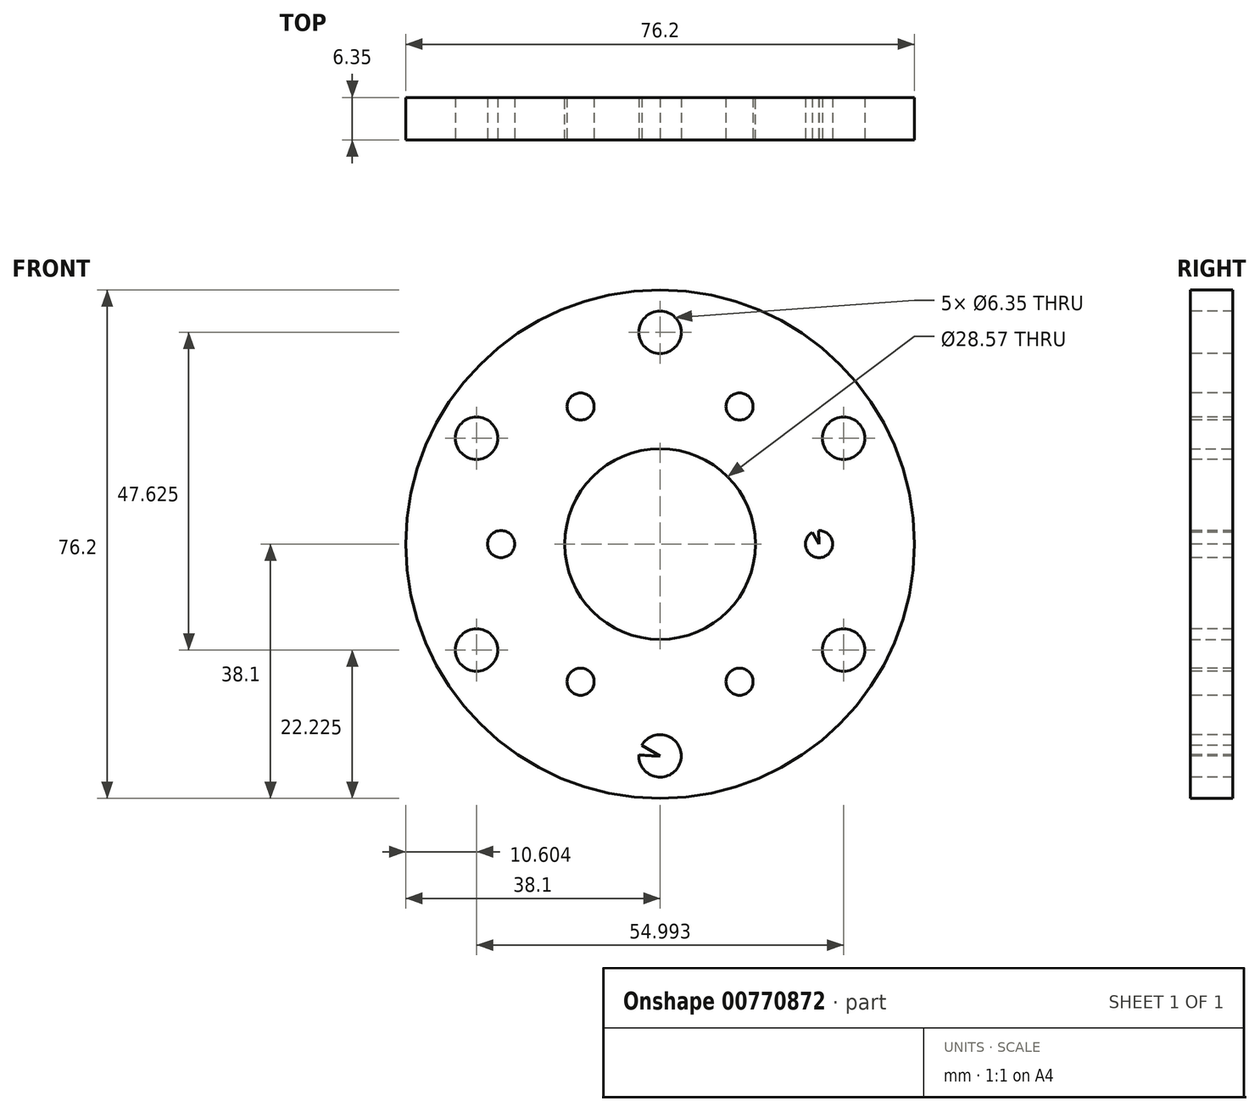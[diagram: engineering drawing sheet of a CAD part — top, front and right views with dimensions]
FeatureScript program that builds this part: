
annotation { "Feature Type Name" : "Feature", "Feature Type Description" : "" }
export const myFeature = defineFeature(function(context is Context, id is Id, definition is map)
    precondition{}
    {
        {
            var Q0;
            Q0=qCreatedBy(makeId("Front.planeOp"),FACE);
            var sketch = newSketch(context, id + "F0", { "sketchPlane" : qUnion([Q0])});
            skCircle(sketch, "E0", {"center": v(0, 0) * mm, "radius": 14.29 * mm});
            skCircle(sketch, "E1", {"center": v(0, 0) * mm, "radius": 38.1 * mm});
            skSolve(sketch);
        }
        {
            var Q0;
            Q0 = qSketchRegion(id + "F0", true);
            extrude(context, id + "F1", {"entities" : qUnion([Q0]), "depth" : 6.35 * mm, "offsetDistance" : 25.4 * mm});
        }
        {
            var Q0;
            Q0=makeQuery(id+"F1.opExtrude","CAP_FACE",FACE,{"disambiguationData":[OSD([sQuery(id+"F0.wireOp",EDGE,"E0"),sQuery(id+"F0.wireOp",EDGE,"E1")])],"isStart":false});
            var sketch = newSketch(context, id + "F2", { "sketchPlane" : qUnion([Q0])});
            skCircle(sketch, "E2", {"center": v(0, 0) * mm, "radius": 23.81 * mm});
            skCircle(sketch, "E3", {"center": v(0, 0) * mm, "radius": 31.75 * mm});
            skCircle(sketch, "E4.cCircle", {"center": v(0, 0) * mm, "radius": 31.75 * mm, "construction": true});
            skLineSegment(sketch, "E4.0", {"start": v(0, 31.75) * mm, "end": v(27.5, 15.88) * mm});
            skLineSegment(sketch, "E4.1", {"start": v(27.5, 15.88) * mm, "end": v(27.5, -15.87) * mm});
            skLineSegment(sketch, "E4.2", {"start": v(27.5, -15.87) * mm, "end": v(0, -31.75) * mm});
            skLineSegment(sketch, "E4.3", {"start": v(0, -31.75) * mm, "end": v(-27.5, -15.88) * mm});
            skLineSegment(sketch, "E4.4", {"start": v(-27.5, -15.88) * mm, "end": v(-27.5, 15.87) * mm});
            skLineSegment(sketch, "E4.5", {"start": v(-27.5, 15.87) * mm, "end": v(0, 31.75) * mm});
            skCircle(sketch, "E5.cCircle", {"center": v(0, 0) * mm, "radius": 23.81 * mm, "construction": true});
            skLineSegment(sketch, "E5.0", {"start": v(-23.81, 0) * mm, "end": v(-11.9, 20.62) * mm});
            skLineSegment(sketch, "E5.1", {"start": v(-11.9, 20.62) * mm, "end": v(11.9, 20.62) * mm});
            skLineSegment(sketch, "E5.2", {"start": v(11.9, 20.62) * mm, "end": v(23.81, 0) * mm});
            skLineSegment(sketch, "E5.3", {"start": v(23.81, 0) * mm, "end": v(11.9, -20.62) * mm});
            skLineSegment(sketch, "E5.4", {"start": v(11.9, -20.62) * mm, "end": v(-11.9, -20.62) * mm});
            skLineSegment(sketch, "E5.5", {"start": v(-11.9, -20.62) * mm, "end": v(-23.81, 0) * mm});
            skCircle(sketch, "E6", {"center": v(0, 31.75) * mm, "radius": 3.18 * mm});
            skCircle(sketch, "E7", {"center": v(27.5, 15.88) * mm, "radius": 3.18 * mm});
            skCircle(sketch, "E8", {"center": v(27.5, -15.87) * mm, "radius": 3.18 * mm});
            skCircle(sketch, "E9", {"center": v(0, -31.75) * mm, "radius": 3.18 * mm});
            skCircle(sketch, "E10", {"center": v(-27.5, -15.88) * mm, "radius": 3.18 * mm});
            skCircle(sketch, "E11", {"center": v(-27.5, 15.87) * mm, "radius": 3.18 * mm});
            skCircle(sketch, "E12", {"center": v(-11.9, 20.62) * mm, "radius": 2.03 * mm});
            skCircle(sketch, "E13", {"center": v(11.9, 20.62) * mm, "radius": 2.03 * mm});
            skCircle(sketch, "E14", {"center": v(23.81, 0) * mm, "radius": 2.03 * mm});
            skCircle(sketch, "E15", {"center": v(11.9, -20.62) * mm, "radius": 2.03 * mm});
            skCircle(sketch, "E16", {"center": v(-11.9, -20.62) * mm, "radius": 2.03 * mm});
            skCircle(sketch, "E17", {"center": v(-23.81, 0) * mm, "radius": 2.03 * mm});
            skSolve(sketch);
        }
        {
            var Q0;
            {var subQ0=sQuery(id+"F2.wireOp",EDGE,"E3");var subQ2=sQuery(id+"F2.wireOp",EDGE,"E7");var subQ3=makeQuery(id+"F2.imprint","INTERSECT",VERTEX,{"disambiguationData":[OD(0.0)],"derivedFrom":[subQ0,subQ2]});Q0=makeQuery(id+"F2.imprint","IMPRINT",FACE,{"disambiguationData":[TD([[makeQuery(id+"F2.imprint","IMPRINT",EDGE,{"disambiguationData":[TD([[subQ3,-1.0]])],"derivedFrom":subQ2}),1.0]])]});}
            var Q1;
            {var subQ1=sQuery(id+"F2.wireOp",EDGE,"E3");var subQ3=sQuery(id+"F2.wireOp",EDGE,"E7");var subQ4=makeQuery(id+"F2.imprint","INTERSECT",VERTEX,{"disambiguationData":[OD(0.0)],"derivedFrom":[subQ1,subQ3]});Q1=makeQuery(id+"F2.imprint","IMPRINT",FACE,{"disambiguationData":[TD([[makeQuery(id+"F2.imprint","IMPRINT",EDGE,{"disambiguationData":[TD([[subQ4,1.0]])],"derivedFrom":subQ3}),1.0]])]});}
            var Q2;
            {var subQ1=sQuery(id+"F2.wireOp",EDGE,"E3");var subQ3=sQuery(id+"F2.wireOp",EDGE,"E7");var subQ4=makeQuery(id+"F2.imprint","INTERSECT",VERTEX,{"disambiguationData":[OD(1.0)],"derivedFrom":[subQ1,subQ3]});Q2=makeQuery(id+"F2.imprint","IMPRINT",FACE,{"disambiguationData":[TD([[makeQuery(id+"F2.imprint","IMPRINT",EDGE,{"disambiguationData":[TD([[subQ4,-1.0]])],"derivedFrom":subQ3}),1.0]])]});}
            var Q3;
            {var subQ0=sQuery(id+"F2.wireOp",EDGE,"E3");var subQ2=sQuery(id+"F2.wireOp",EDGE,"E6");var subQ3=makeQuery(id+"F2.imprint","INTERSECT",VERTEX,{"disambiguationData":[OD(0.0)],"derivedFrom":[subQ0,subQ2]});Q3=makeQuery(id+"F2.imprint","IMPRINT",FACE,{"disambiguationData":[TD([[makeQuery(id+"F2.imprint","IMPRINT",EDGE,{"disambiguationData":[TD([[subQ3,-1.0]])],"derivedFrom":subQ2}),1.0]])]});}
            var Q4;
            {var subQ1=sQuery(id+"F2.wireOp",EDGE,"E3");var subQ3=sQuery(id+"F2.wireOp",EDGE,"E6");var subQ4=makeQuery(id+"F2.imprint","INTERSECT",VERTEX,{"disambiguationData":[OD(0.0)],"derivedFrom":[subQ1,subQ3]});Q4=makeQuery(id+"F2.imprint","IMPRINT",FACE,{"disambiguationData":[TD([[makeQuery(id+"F2.imprint","IMPRINT",EDGE,{"disambiguationData":[TD([[subQ4,1.0]])],"derivedFrom":subQ3}),1.0]])]});}
            var Q5;
            {var subQ1=sQuery(id+"F2.wireOp",EDGE,"E3");var subQ3=sQuery(id+"F2.wireOp",EDGE,"E6");var subQ4=makeQuery(id+"F2.imprint","INTERSECT",VERTEX,{"disambiguationData":[OD(1.0)],"derivedFrom":[subQ1,subQ3]});Q5=makeQuery(id+"F2.imprint","IMPRINT",FACE,{"disambiguationData":[TD([[makeQuery(id+"F2.imprint","IMPRINT",EDGE,{"disambiguationData":[TD([[subQ4,-1.0]])],"derivedFrom":subQ3}),1.0]])]});}
            var Q6;
            {var subQ0=sQuery(id+"F2.wireOp",EDGE,"E3");var subQ2=sQuery(id+"F2.wireOp",EDGE,"E11");var subQ3=makeQuery(id+"F2.imprint","INTERSECT",VERTEX,{"disambiguationData":[OD(0.0)],"derivedFrom":[subQ0,subQ2]});Q6=makeQuery(id+"F2.imprint","IMPRINT",FACE,{"disambiguationData":[TD([[makeQuery(id+"F2.imprint","IMPRINT",EDGE,{"disambiguationData":[TD([[subQ3,-1.0]])],"derivedFrom":subQ2}),1.0]])]});}
            var Q7;
            {var subQ1=sQuery(id+"F2.wireOp",EDGE,"E3");var subQ3=sQuery(id+"F2.wireOp",EDGE,"E11");var subQ4=makeQuery(id+"F2.imprint","INTERSECT",VERTEX,{"disambiguationData":[OD(0.0)],"derivedFrom":[subQ1,subQ3]});Q7=makeQuery(id+"F2.imprint","IMPRINT",FACE,{"disambiguationData":[TD([[makeQuery(id+"F2.imprint","IMPRINT",EDGE,{"disambiguationData":[TD([[subQ4,1.0]])],"derivedFrom":subQ3}),1.0]])]});}
            var Q8;
            {var subQ1=sQuery(id+"F2.wireOp",EDGE,"E3");var subQ3=sQuery(id+"F2.wireOp",EDGE,"E11");var subQ4=makeQuery(id+"F2.imprint","INTERSECT",VERTEX,{"disambiguationData":[OD(1.0)],"derivedFrom":[subQ1,subQ3]});Q8=makeQuery(id+"F2.imprint","IMPRINT",FACE,{"disambiguationData":[TD([[makeQuery(id+"F2.imprint","IMPRINT",EDGE,{"disambiguationData":[TD([[subQ4,-1.0]])],"derivedFrom":subQ3}),1.0]])]});}
            var Q9;
            {var subQ0=sQuery(id+"F2.wireOp",EDGE,"E3");var subQ2=sQuery(id+"F2.wireOp",EDGE,"E10");var subQ3=makeQuery(id+"F2.imprint","INTERSECT",VERTEX,{"disambiguationData":[OD(0.0)],"derivedFrom":[subQ0,subQ2]});Q9=makeQuery(id+"F2.imprint","IMPRINT",FACE,{"disambiguationData":[TD([[makeQuery(id+"F2.imprint","IMPRINT",EDGE,{"disambiguationData":[TD([[subQ3,-1.0]])],"derivedFrom":subQ2}),1.0]])]});}
            var Q10;
            {var subQ1=sQuery(id+"F2.wireOp",EDGE,"E3");var subQ3=sQuery(id+"F2.wireOp",EDGE,"E10");var subQ4=makeQuery(id+"F2.imprint","INTERSECT",VERTEX,{"disambiguationData":[OD(0.0)],"derivedFrom":[subQ1,subQ3]});Q10=makeQuery(id+"F2.imprint","IMPRINT",FACE,{"disambiguationData":[TD([[makeQuery(id+"F2.imprint","IMPRINT",EDGE,{"disambiguationData":[TD([[subQ4,1.0]])],"derivedFrom":subQ3}),1.0]])]});}
            var Q11;
            {var subQ1=sQuery(id+"F2.wireOp",EDGE,"E3");var subQ3=sQuery(id+"F2.wireOp",EDGE,"E10");var subQ4=makeQuery(id+"F2.imprint","INTERSECT",VERTEX,{"disambiguationData":[OD(1.0)],"derivedFrom":[subQ1,subQ3]});Q11=makeQuery(id+"F2.imprint","IMPRINT",FACE,{"disambiguationData":[TD([[makeQuery(id+"F2.imprint","IMPRINT",EDGE,{"disambiguationData":[TD([[subQ4,-1.0]])],"derivedFrom":subQ3}),1.0]])]});}
            var Q12;
            {var subQ0=sQuery(id+"F2.wireOp",EDGE,"E3");var subQ2=sQuery(id+"F2.wireOp",EDGE,"E9");var subQ3=makeQuery(id+"F2.imprint","INTERSECT",VERTEX,{"disambiguationData":[OD(0.0)],"derivedFrom":[subQ0,subQ2]});Q12=makeQuery(id+"F2.imprint","IMPRINT",FACE,{"disambiguationData":[TD([[makeQuery(id+"F2.imprint","IMPRINT",EDGE,{"disambiguationData":[TD([[subQ3,-1.0]])],"derivedFrom":subQ2}),1.0]])]});}
            var Q13;
            {var subQ1=sQuery(id+"F2.wireOp",EDGE,"E3");var subQ3=sQuery(id+"F2.wireOp",EDGE,"E9");var subQ4=makeQuery(id+"F2.imprint","INTERSECT",VERTEX,{"disambiguationData":[OD(0.0)],"derivedFrom":[subQ1,subQ3]});Q13=makeQuery(id+"F2.imprint","IMPRINT",FACE,{"disambiguationData":[TD([[makeQuery(id+"F2.imprint","IMPRINT",EDGE,{"disambiguationData":[TD([[subQ4,1.0]])],"derivedFrom":subQ3}),1.0]])]});}
            var Q14;
            {var subQ1=sQuery(id+"F2.wireOp",EDGE,"E3");var subQ3=sQuery(id+"F2.wireOp",EDGE,"E9");var subQ4=makeQuery(id+"F2.imprint","INTERSECT",VERTEX,{"disambiguationData":[OD(1.0)],"derivedFrom":[subQ1,subQ3]});Q14=makeQuery(id+"F2.imprint","IMPRINT",FACE,{"disambiguationData":[TD([[makeQuery(id+"F2.imprint","IMPRINT",EDGE,{"disambiguationData":[TD([[subQ4,-1.0]])],"derivedFrom":subQ3}),1.0]])]});}
            var Q15;
            {var subQ0=sQuery(id+"F2.wireOp",EDGE,"E3");var subQ2=sQuery(id+"F2.wireOp",EDGE,"E8");var subQ3=makeQuery(id+"F2.imprint","INTERSECT",VERTEX,{"disambiguationData":[OD(0.0)],"derivedFrom":[subQ0,subQ2]});Q15=makeQuery(id+"F2.imprint","IMPRINT",FACE,{"disambiguationData":[TD([[makeQuery(id+"F2.imprint","IMPRINT",EDGE,{"disambiguationData":[TD([[subQ3,-1.0]])],"derivedFrom":subQ2}),1.0]])]});}
            var Q16;
            {var subQ1=sQuery(id+"F2.wireOp",EDGE,"E3");var subQ3=sQuery(id+"F2.wireOp",EDGE,"E8");var subQ4=makeQuery(id+"F2.imprint","INTERSECT",VERTEX,{"disambiguationData":[OD(0.0)],"derivedFrom":[subQ1,subQ3]});Q16=makeQuery(id+"F2.imprint","IMPRINT",FACE,{"disambiguationData":[TD([[makeQuery(id+"F2.imprint","IMPRINT",EDGE,{"disambiguationData":[TD([[subQ4,1.0]])],"derivedFrom":subQ3}),1.0]])]});}
            var Q17;
            {var subQ1=sQuery(id+"F2.wireOp",EDGE,"E3");var subQ3=sQuery(id+"F2.wireOp",EDGE,"E8");var subQ4=makeQuery(id+"F2.imprint","INTERSECT",VERTEX,{"disambiguationData":[OD(1.0)],"derivedFrom":[subQ1,subQ3]});Q17=makeQuery(id+"F2.imprint","IMPRINT",FACE,{"disambiguationData":[TD([[makeQuery(id+"F2.imprint","IMPRINT",EDGE,{"disambiguationData":[TD([[subQ4,-1.0]])],"derivedFrom":subQ3}),1.0]])]});}
            var Q18;
            {var subQ1=sQuery(id+"F2.wireOp",EDGE,"E4.4");var subQ3=sQuery(id+"F2.wireOp",EDGE,"E11");var subQ4=makeQuery(id+"F2.imprint","INTERSECT",VERTEX,{"derivedFrom":[subQ1,subQ3]});Q18=makeQuery(id+"F2.imprint","IMPRINT",FACE,{"disambiguationData":[TD([[makeQuery(id+"F2.imprint","IMPRINT",EDGE,{"disambiguationData":[TD([[subQ4,-1.0]])],"derivedFrom":subQ3}),1.0]])]});}
            var Q19;
            {var subQ1=sQuery(id+"F2.wireOp",EDGE,"E4.3");var subQ3=sQuery(id+"F2.wireOp",EDGE,"E10");var subQ4=makeQuery(id+"F2.imprint","INTERSECT",VERTEX,{"derivedFrom":[subQ1,subQ3]});Q19=makeQuery(id+"F2.imprint","IMPRINT",FACE,{"disambiguationData":[TD([[makeQuery(id+"F2.imprint","IMPRINT",EDGE,{"disambiguationData":[TD([[subQ4,-1.0]])],"derivedFrom":subQ3}),1.0]])]});}
            var Q20;
            {var subQ1=sQuery(id+"F2.wireOp",EDGE,"E4.2");var subQ3=sQuery(id+"F2.wireOp",EDGE,"E9");var subQ4=makeQuery(id+"F2.imprint","INTERSECT",VERTEX,{"derivedFrom":[subQ1,subQ3]});Q20=makeQuery(id+"F2.imprint","IMPRINT",FACE,{"disambiguationData":[TD([[makeQuery(id+"F2.imprint","IMPRINT",EDGE,{"disambiguationData":[TD([[subQ4,-1.0]])],"derivedFrom":subQ3}),1.0]])]});}
            var Q21;
            {var subQ1=sQuery(id+"F2.wireOp",EDGE,"E4.1");var subQ3=sQuery(id+"F2.wireOp",EDGE,"E8");var subQ4=makeQuery(id+"F2.imprint","INTERSECT",VERTEX,{"derivedFrom":[subQ1,subQ3]});Q21=makeQuery(id+"F2.imprint","IMPRINT",FACE,{"disambiguationData":[TD([[makeQuery(id+"F2.imprint","IMPRINT",EDGE,{"disambiguationData":[TD([[subQ4,-1.0]])],"derivedFrom":subQ3}),1.0]])]});}
            var Q22;
            {var subQ1=sQuery(id+"F2.wireOp",EDGE,"E4.0");var subQ3=sQuery(id+"F2.wireOp",EDGE,"E7");var subQ4=makeQuery(id+"F2.imprint","INTERSECT",VERTEX,{"derivedFrom":[subQ1,subQ3]});Q22=makeQuery(id+"F2.imprint","IMPRINT",FACE,{"disambiguationData":[TD([[makeQuery(id+"F2.imprint","IMPRINT",EDGE,{"disambiguationData":[TD([[subQ4,-1.0]])],"derivedFrom":subQ3}),1.0]])]});}
            var Q23;
            {var subQ1=sQuery(id+"F2.wireOp",EDGE,"E4.0");var subQ3=sQuery(id+"F2.wireOp",EDGE,"E6");var subQ4=makeQuery(id+"F2.imprint","INTERSECT",VERTEX,{"derivedFrom":[subQ1,subQ3]});Q23=makeQuery(id+"F2.imprint","IMPRINT",FACE,{"disambiguationData":[TD([[makeQuery(id+"F2.imprint","IMPRINT",EDGE,{"disambiguationData":[TD([[subQ4,1.0]])],"derivedFrom":subQ3}),1.0]])]});}
            var Q24;
            {var subQ0=sQuery(id+"F2.wireOp",EDGE,"E2");var subQ2=sQuery(id+"F2.wireOp",EDGE,"E12");var subQ3=makeQuery(id+"F2.imprint","INTERSECT",VERTEX,{"disambiguationData":[OD(0.0)],"derivedFrom":[subQ0,subQ2]});Q24=makeQuery(id+"F2.imprint","IMPRINT",FACE,{"disambiguationData":[TD([[makeQuery(id+"F2.imprint","IMPRINT",EDGE,{"disambiguationData":[TD([[subQ3,-1.0]])],"derivedFrom":subQ2}),1.0]])]});}
            var Q25;
            {var subQ1=sQuery(id+"F2.wireOp",EDGE,"E5.0");var subQ3=sQuery(id+"F2.wireOp",EDGE,"E12");var subQ4=makeQuery(id+"F2.imprint","INTERSECT",VERTEX,{"derivedFrom":[subQ1,subQ3]});Q25=makeQuery(id+"F2.imprint","IMPRINT",FACE,{"disambiguationData":[TD([[makeQuery(id+"F2.imprint","IMPRINT",EDGE,{"disambiguationData":[TD([[subQ4,-1.0]])],"derivedFrom":subQ3}),1.0]])]});}
            var Q26;
            {var subQ1=sQuery(id+"F2.wireOp",EDGE,"E2");var subQ3=sQuery(id+"F2.wireOp",EDGE,"E12");var subQ4=makeQuery(id+"F2.imprint","INTERSECT",VERTEX,{"disambiguationData":[OD(0.0)],"derivedFrom":[subQ1,subQ3]});Q26=makeQuery(id+"F2.imprint","IMPRINT",FACE,{"disambiguationData":[TD([[makeQuery(id+"F2.imprint","IMPRINT",EDGE,{"disambiguationData":[TD([[subQ4,1.0]])],"derivedFrom":subQ3}),1.0]])]});}
            var Q27;
            {var subQ1=sQuery(id+"F2.wireOp",EDGE,"E2");var subQ3=sQuery(id+"F2.wireOp",EDGE,"E12");var subQ4=makeQuery(id+"F2.imprint","INTERSECT",VERTEX,{"disambiguationData":[OD(1.0)],"derivedFrom":[subQ1,subQ3]});Q27=makeQuery(id+"F2.imprint","IMPRINT",FACE,{"disambiguationData":[TD([[makeQuery(id+"F2.imprint","IMPRINT",EDGE,{"disambiguationData":[TD([[subQ4,-1.0]])],"derivedFrom":subQ3}),1.0]])]});}
            var Q28;
            {var subQ1=sQuery(id+"F2.wireOp",EDGE,"E2");var subQ3=sQuery(id+"F2.wireOp",EDGE,"E13");var subQ4=makeQuery(id+"F2.imprint","INTERSECT",VERTEX,{"disambiguationData":[OD(1.0)],"derivedFrom":[subQ1,subQ3]});Q28=makeQuery(id+"F2.imprint","IMPRINT",FACE,{"disambiguationData":[TD([[makeQuery(id+"F2.imprint","IMPRINT",EDGE,{"disambiguationData":[TD([[subQ4,-1.0]])],"derivedFrom":subQ3}),1.0]])]});}
            var Q29;
            {var subQ0=sQuery(id+"F2.wireOp",EDGE,"E2");var subQ2=sQuery(id+"F2.wireOp",EDGE,"E13");var subQ3=makeQuery(id+"F2.imprint","INTERSECT",VERTEX,{"disambiguationData":[OD(0.0)],"derivedFrom":[subQ0,subQ2]});Q29=makeQuery(id+"F2.imprint","IMPRINT",FACE,{"disambiguationData":[TD([[makeQuery(id+"F2.imprint","IMPRINT",EDGE,{"disambiguationData":[TD([[subQ3,-1.0]])],"derivedFrom":subQ2}),1.0]])]});}
            var Q30;
            {var subQ1=sQuery(id+"F2.wireOp",EDGE,"E5.1");var subQ3=sQuery(id+"F2.wireOp",EDGE,"E13");var subQ4=makeQuery(id+"F2.imprint","INTERSECT",VERTEX,{"derivedFrom":[subQ1,subQ3]});Q30=makeQuery(id+"F2.imprint","IMPRINT",FACE,{"disambiguationData":[TD([[makeQuery(id+"F2.imprint","IMPRINT",EDGE,{"disambiguationData":[TD([[subQ4,-1.0]])],"derivedFrom":subQ3}),1.0]])]});}
            var Q31;
            {var subQ1=sQuery(id+"F2.wireOp",EDGE,"E2");var subQ3=sQuery(id+"F2.wireOp",EDGE,"E13");var subQ4=makeQuery(id+"F2.imprint","INTERSECT",VERTEX,{"disambiguationData":[OD(0.0)],"derivedFrom":[subQ1,subQ3]});Q31=makeQuery(id+"F2.imprint","IMPRINT",FACE,{"disambiguationData":[TD([[makeQuery(id+"F2.imprint","IMPRINT",EDGE,{"disambiguationData":[TD([[subQ4,1.0]])],"derivedFrom":subQ3}),1.0]])]});}
            var Q32;
            {var subQ1=sQuery(id+"F2.wireOp",EDGE,"E5.3");var subQ3=sQuery(id+"F2.wireOp",EDGE,"E15");var subQ4=makeQuery(id+"F2.imprint","INTERSECT",VERTEX,{"derivedFrom":[subQ1,subQ3]});Q32=makeQuery(id+"F2.imprint","IMPRINT",FACE,{"disambiguationData":[TD([[makeQuery(id+"F2.imprint","IMPRINT",EDGE,{"disambiguationData":[TD([[subQ4,-1.0]])],"derivedFrom":subQ3}),1.0]])]});}
            var Q33;
            {var subQ0=sQuery(id+"F2.wireOp",EDGE,"E2");var subQ2=sQuery(id+"F2.wireOp",EDGE,"E15");var subQ3=makeQuery(id+"F2.imprint","INTERSECT",VERTEX,{"disambiguationData":[OD(0.0)],"derivedFrom":[subQ0,subQ2]});Q33=makeQuery(id+"F2.imprint","IMPRINT",FACE,{"disambiguationData":[TD([[makeQuery(id+"F2.imprint","IMPRINT",EDGE,{"disambiguationData":[TD([[subQ3,-1.0]])],"derivedFrom":subQ2}),1.0]])]});}
            var Q34;
            {var subQ1=sQuery(id+"F2.wireOp",EDGE,"E2");var subQ3=sQuery(id+"F2.wireOp",EDGE,"E15");var subQ4=makeQuery(id+"F2.imprint","INTERSECT",VERTEX,{"disambiguationData":[OD(1.0)],"derivedFrom":[subQ1,subQ3]});Q34=makeQuery(id+"F2.imprint","IMPRINT",FACE,{"disambiguationData":[TD([[makeQuery(id+"F2.imprint","IMPRINT",EDGE,{"disambiguationData":[TD([[subQ4,-1.0]])],"derivedFrom":subQ3}),1.0]])]});}
            var Q35;
            {var subQ1=sQuery(id+"F2.wireOp",EDGE,"E2");var subQ3=sQuery(id+"F2.wireOp",EDGE,"E15");var subQ4=makeQuery(id+"F2.imprint","INTERSECT",VERTEX,{"disambiguationData":[OD(0.0)],"derivedFrom":[subQ1,subQ3]});Q35=makeQuery(id+"F2.imprint","IMPRINT",FACE,{"disambiguationData":[TD([[makeQuery(id+"F2.imprint","IMPRINT",EDGE,{"disambiguationData":[TD([[subQ4,1.0]])],"derivedFrom":subQ3}),1.0]])]});}
            var Q36;
            {var subQ0=sQuery(id+"F2.wireOp",EDGE,"E2");var subQ2=sQuery(id+"F2.wireOp",EDGE,"E16");var subQ3=makeQuery(id+"F2.imprint","INTERSECT",VERTEX,{"disambiguationData":[OD(0.0)],"derivedFrom":[subQ0,subQ2]});Q36=makeQuery(id+"F2.imprint","IMPRINT",FACE,{"disambiguationData":[TD([[makeQuery(id+"F2.imprint","IMPRINT",EDGE,{"disambiguationData":[TD([[subQ3,-1.0]])],"derivedFrom":subQ2}),1.0]])]});}
            var Q37;
            {var subQ1=sQuery(id+"F2.wireOp",EDGE,"E2");var subQ3=sQuery(id+"F2.wireOp",EDGE,"E16");var subQ4=makeQuery(id+"F2.imprint","INTERSECT",VERTEX,{"disambiguationData":[OD(1.0)],"derivedFrom":[subQ1,subQ3]});Q37=makeQuery(id+"F2.imprint","IMPRINT",FACE,{"disambiguationData":[TD([[makeQuery(id+"F2.imprint","IMPRINT",EDGE,{"disambiguationData":[TD([[subQ4,-1.0]])],"derivedFrom":subQ3}),1.0]])]});}
            var Q38;
            {var subQ1=sQuery(id+"F2.wireOp",EDGE,"E5.4");var subQ3=sQuery(id+"F2.wireOp",EDGE,"E16");var subQ4=makeQuery(id+"F2.imprint","INTERSECT",VERTEX,{"derivedFrom":[subQ1,subQ3]});Q38=makeQuery(id+"F2.imprint","IMPRINT",FACE,{"disambiguationData":[TD([[makeQuery(id+"F2.imprint","IMPRINT",EDGE,{"disambiguationData":[TD([[subQ4,-1.0]])],"derivedFrom":subQ3}),1.0]])]});}
            var Q39;
            {var subQ1=sQuery(id+"F2.wireOp",EDGE,"E2");var subQ3=sQuery(id+"F2.wireOp",EDGE,"E16");var subQ4=makeQuery(id+"F2.imprint","INTERSECT",VERTEX,{"disambiguationData":[OD(0.0)],"derivedFrom":[subQ1,subQ3]});Q39=makeQuery(id+"F2.imprint","IMPRINT",FACE,{"disambiguationData":[TD([[makeQuery(id+"F2.imprint","IMPRINT",EDGE,{"disambiguationData":[TD([[subQ4,1.0]])],"derivedFrom":subQ3}),1.0]])]});}
            var Q40;
            {var subQ1=sQuery(id+"F2.wireOp",EDGE,"E2");var subQ3=sQuery(id+"F2.wireOp",EDGE,"E17");var subQ4=makeQuery(id+"F2.imprint","INTERSECT",VERTEX,{"disambiguationData":[OD(0.0)],"derivedFrom":[subQ1,subQ3]});Q40=makeQuery(id+"F2.imprint","IMPRINT",FACE,{"disambiguationData":[TD([[makeQuery(id+"F2.imprint","IMPRINT",EDGE,{"disambiguationData":[TD([[subQ4,1.0]])],"derivedFrom":subQ3}),1.0]])]});}
            var Q41;
            {var subQ1=sQuery(id+"F2.wireOp",EDGE,"E5.0");var subQ3=sQuery(id+"F2.wireOp",EDGE,"E17");var subQ4=makeQuery(id+"F2.imprint","INTERSECT",VERTEX,{"derivedFrom":[subQ1,subQ3]});Q41=makeQuery(id+"F2.imprint","IMPRINT",FACE,{"disambiguationData":[TD([[makeQuery(id+"F2.imprint","IMPRINT",EDGE,{"disambiguationData":[TD([[subQ4,1.0]])],"derivedFrom":subQ3}),1.0]])]});}
            var Q42;
            {var subQ1=sQuery(id+"F2.wireOp",EDGE,"E2");var subQ3=sQuery(id+"F2.wireOp",EDGE,"E17");var subQ4=makeQuery(id+"F2.imprint","INTERSECT",VERTEX,{"disambiguationData":[OD(1.0)],"derivedFrom":[subQ1,subQ3]});Q42=makeQuery(id+"F2.imprint","IMPRINT",FACE,{"disambiguationData":[TD([[makeQuery(id+"F2.imprint","IMPRINT",EDGE,{"disambiguationData":[TD([[subQ4,-1.0]])],"derivedFrom":subQ3}),1.0]])]});}
            var Q43;
            {var subQ0=sQuery(id+"F2.wireOp",EDGE,"E2");var subQ2=sQuery(id+"F2.wireOp",EDGE,"E17");var subQ3=makeQuery(id+"F2.imprint","INTERSECT",VERTEX,{"disambiguationData":[OD(0.0)],"derivedFrom":[subQ0,subQ2]});Q43=makeQuery(id+"F2.imprint","IMPRINT",FACE,{"disambiguationData":[TD([[makeQuery(id+"F2.imprint","IMPRINT",EDGE,{"disambiguationData":[TD([[subQ3,-1.0]])],"derivedFrom":subQ2}),1.0]])]});}
            var Q44;
            {var subQ0=sQuery(id+"F2.wireOp",EDGE,"E2");var subQ2=sQuery(id+"F2.wireOp",EDGE,"E14");var subQ3=makeQuery(id+"F2.imprint","INTERSECT",VERTEX,{"disambiguationData":[OD(0.0)],"derivedFrom":[subQ0,subQ2]});Q44=makeQuery(id+"F2.imprint","IMPRINT",FACE,{"disambiguationData":[TD([[makeQuery(id+"F2.imprint","IMPRINT",EDGE,{"disambiguationData":[TD([[subQ3,1.0]])],"derivedFrom":subQ2}),1.0]])]});}
            var Q45;
            {var subQ1=sQuery(id+"F2.wireOp",EDGE,"E2");var subQ3=sQuery(id+"F2.wireOp",EDGE,"E14");var subQ4=makeQuery(id+"F2.imprint","INTERSECT",VERTEX,{"disambiguationData":[OD(0.0)],"derivedFrom":[subQ1,subQ3]});Q45=makeQuery(id+"F2.imprint","IMPRINT",FACE,{"disambiguationData":[TD([[makeQuery(id+"F2.imprint","IMPRINT",EDGE,{"disambiguationData":[TD([[subQ4,-1.0]])],"derivedFrom":subQ3}),1.0]])]});}
            var Q46;
            {var subQ1=sQuery(id+"F2.wireOp",EDGE,"E5.2");var subQ3=sQuery(id+"F2.wireOp",EDGE,"E14");var subQ4=makeQuery(id+"F2.imprint","INTERSECT",VERTEX,{"derivedFrom":[subQ1,subQ3]});Q46=makeQuery(id+"F2.imprint","IMPRINT",FACE,{"disambiguationData":[TD([[makeQuery(id+"F2.imprint","IMPRINT",EDGE,{"disambiguationData":[TD([[subQ4,-1.0]])],"derivedFrom":subQ3}),1.0]])]});}
            var Q47;
            {var subQ1=sQuery(id+"F2.wireOp",EDGE,"E2");var subQ3=sQuery(id+"F2.wireOp",EDGE,"E14");var subQ4=makeQuery(id+"F2.imprint","INTERSECT",VERTEX,{"disambiguationData":[OD(1.0)],"derivedFrom":[subQ1,subQ3]});Q47=makeQuery(id+"F2.imprint","IMPRINT",FACE,{"disambiguationData":[TD([[makeQuery(id+"F2.imprint","IMPRINT",EDGE,{"disambiguationData":[TD([[subQ4,1.0]])],"derivedFrom":subQ3}),1.0]])]});}
            extrude(context, id + "F3", {"entities" : qUnion([Q0, Q1, Q2, Q3, Q4, Q5, Q6, Q7, Q8, Q9, Q10, Q11, Q12, Q13, Q14, Q15, Q16, Q17, Q18, Q19, Q20, Q21, Q22, Q23, Q24, Q25, Q26, Q27, Q28, Q29, Q30, Q31, Q32, Q33, Q34, Q35, Q36, Q37, Q38, Q39, Q40, Q41, Q42, Q43, Q44, Q45, Q46, Q47]), "operationType" : NewBodyOperationType.REMOVE, "endBound" : BoundingType.THROUGH_ALL, "oppositeDirection" : true, "depth" : 25.4 * mm, "offsetDistance" : 25.4 * mm});
        }
    });
